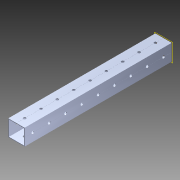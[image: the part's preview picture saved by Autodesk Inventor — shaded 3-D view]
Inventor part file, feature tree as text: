
AUTODESK INVENTOR PART (.ipt)
format: ipt  version: 2014 (Build 180170000, 170)  size: 1,159,680 bytes
history: native  units: in
note: dims shown in document units (in); Inventor stores cm internally (conversion verified against a paired STEP export)
features: pattern_circular x1, other x1, plane x1, extrude x1, imported_body x1, sketch x1
ambient origin geometry x8: Origin, YZ Plane, XZ Plane, XY Plane, X Axis, Y Axis, Z Axis, Center Point
bodies: Body1 (feature_tree)
feature tree (6):
  pattern_circular  "CirPattern2"
  other  "217-3426-STEP1"
  plane  "Work Plane1"
  extrude  "Extrusion1"  Depth=3937.0079in TaperAngle=0.0deg
  imported_body  "Base1"
  sketch  "Sketch1"  dims[d0=-9.0in d1=3937.0079in d2=0.0in]
